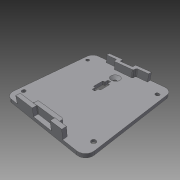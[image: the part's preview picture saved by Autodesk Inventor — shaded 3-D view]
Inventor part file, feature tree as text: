
AUTODESK INVENTOR PART (.ipt)
format: ipt  version: 2014 (Build 180170000, 170)  size: 291,840 bytes
history: native  units: mm
features: sketch x8, extrude x7, fillet x4, hole x1, chamfer x1
ambient origin geometry x8: Origin, YZ Plane, XZ Plane, XY Plane, X Axis, Y Axis, Z Axis, Center Point
bodies: Solid1 (feature_tree)
feature tree (21):
  extrude  "Extrusion1"  Depth=76.0mm
  extrude  "Extrusion2"  Depth=3.0mm
  extrude  "Extrusion3"  Depth=3.0mm
  extrude  "Extrusion4"  Depth=9.0mm
  hole  "Hole1"  [1 undecoded]
  fillet  "Fillet1"  Radius=16.1mm
  extrude  "Extrusion5"  Depth=6.2mm TaperAngle=0.0deg
  fillet  "Fillet2"  Radius=10.0mm
  chamfer  "Chamfer1"  Distance=16.33mm
  extrude  "Extrusion6"  Depth=6.0mm
  extrude  "Extrusion7"  Depth=1.0mm
  fillet  "Fillet3"  Radius=62.48mm
  fillet  "Fillet4"  Radius=6.0mm
  sketch  "Sketch1"  dims[d0=70.0mm d1=76.0mm]
  sketch  "Sketch2"  dims[d2=3.0mm d3=0.0mm d4=13.72mm]
  sketch  "Sketch3"  dims[d5=13.72mm d6=3.0mm]
  sketch  "Sketch4"  dims[d8=6.3mm d9=0.0mm d10=9.0mm]
  sketch  "Sketch5"  dims[d11=3.0mm d14=7.1mm d15=0.0mm d16=16.1mm]
  sketch  "Sketch6"  dims[d17=15.7mm d18=6.2mm d19=0.0mm d20=10.0mm]
  sketch  "Sketch7"  dims[d21=4.5mm]
  sketch  "Sketch8"  dims[d22=3.2mm d23=6.0mm d24=6.0mm d25=1.0mm d26=90.0deg d27=8.0mm d28=20.594885mm d29=16.33mm d30=6.0mm d31=43.94mm d32=62.48mm d33=6.0mm d34=9.0mm d35=2.5mm d36=15.0mm d38=20.32mm d39=3.0mm d40=7.37mm d42=10.0mm d43=0.0mm d44=21.84mm d45=22.35mm d46=0.5mm d47=2.5mm d48=2.0mm d49=45.0deg d50=0.5mm d51=10.0mm d52=0.0mm d53=0.2mm d54=3.0mm d55=3.0mm d56=3.0mm d57=3.0mm d58=3.0mm d59=3.0mm d60=10.0mm d61=0.0mm d62=0.5mm d63=1.0mm]
note: 1 required parameter value undecoded (feature->parameter linkage not recoverable at this tier; creation-order binding heuristic only, values carry confidence <= 0.55)
